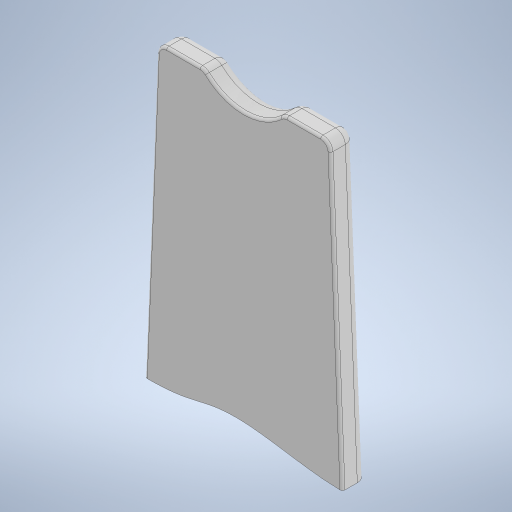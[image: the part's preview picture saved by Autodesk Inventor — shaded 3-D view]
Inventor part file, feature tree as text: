
AUTODESK INVENTOR PART (.ipt)
format: ipt  version: 2023 (Build 270158000, 158)  size: 272,896 bytes
history: native  units: in
note: dims shown in document units (in); Inventor stores cm internally (conversion verified against a paired STEP export)
features: fillet x2, extrude x1, sketch x1
ambient origin geometry x8: Origin, YZ Plane, XZ Plane, XY Plane, X Axis, Y Axis, Z Axis, Center Point
bodies: Solid1 (feature_tree)
feature tree (4):
  extrude  "Extrusion1"  Depth=0.1969in
  fillet  "Fillet1"  Radius=13.7795in
  fillet  "Fillet2"  Radius=15.748in
  sketch  "Sketch1"  dims[d0=23.622in d1=0.9843in d2=13.7795in d3=15.748in d4=6.8898in d5=1.9685in d6=0.0in d7=0.7874in d8=0.1969in]
